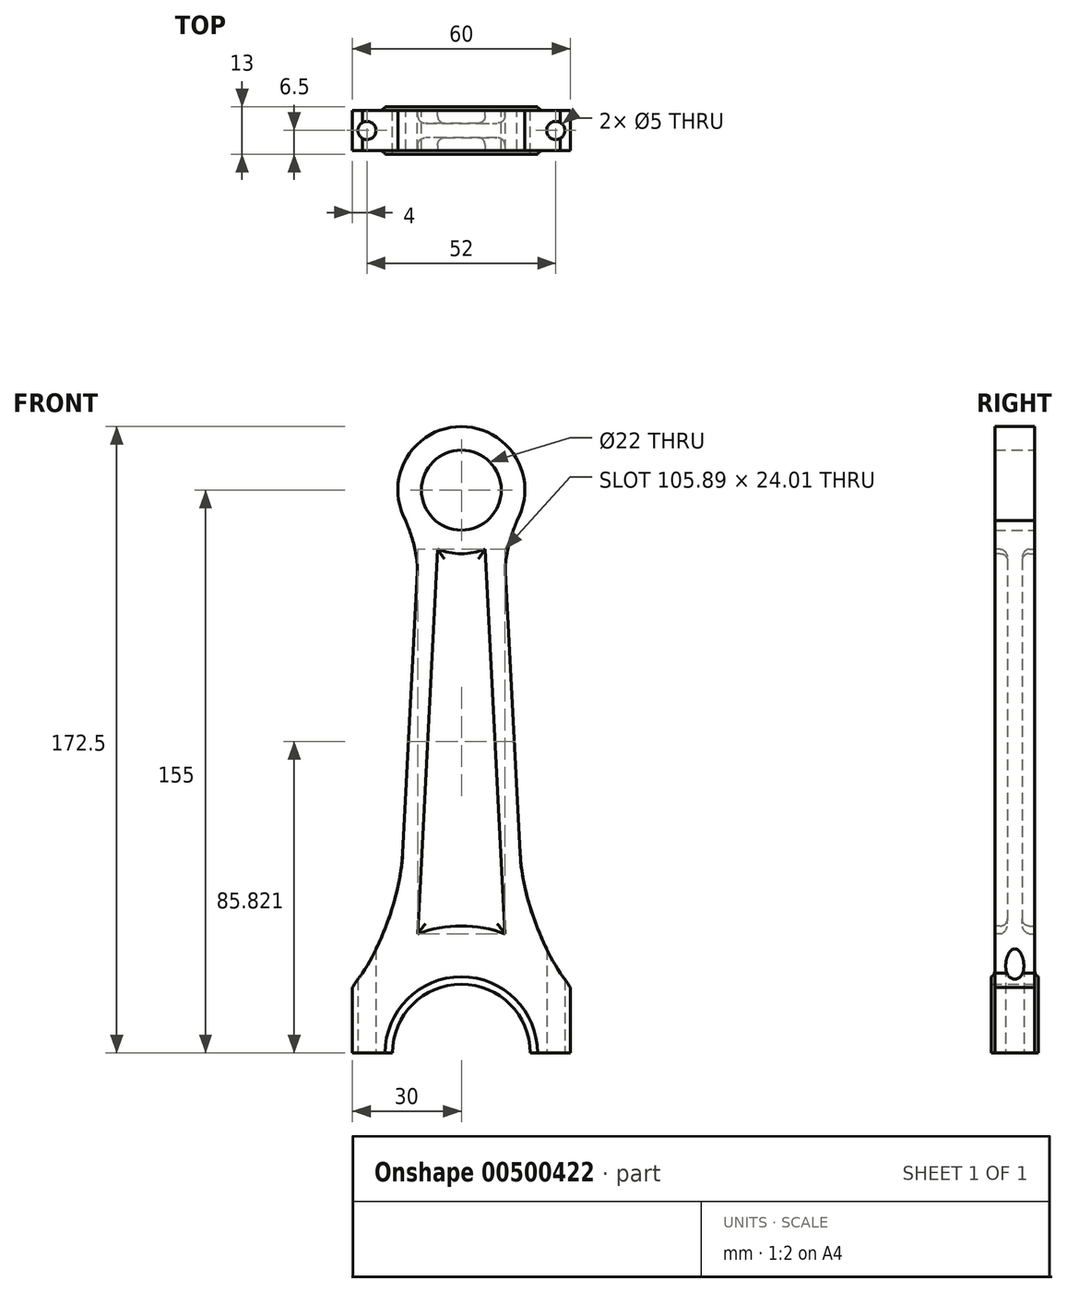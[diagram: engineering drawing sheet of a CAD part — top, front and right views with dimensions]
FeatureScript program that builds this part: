
annotation { "Feature Type Name" : "Feature", "Feature Type Description" : "" }
export const myFeature = defineFeature(function(context is Context, id is Id, definition is map)
    precondition{}
    {
        {
            var Q0;
            Q0=qCreatedBy(makeId("Front.planeOp"),FACE);
            var sketch = newSketch(context, id + "F0", { "sketchPlane" : qUnion([Q0])});
            skCircle(sketch, "E0", {"center": v(0, 121.72) * mm, "radius": 11 * mm});
            skArc(sketch, "E1", {"start": v(19, -33.28) * mm, "mid": v(0, -14.28) * mm, "end": v(-19, -33.28) * mm});
            skLineSegment(sketch, "E2", {"start": v(-11.69, 108.7) * mm, "end": v(-17.46, -2.94) * mm});
            skLineSegment(sketch, "E3", {"start": v(11.69, 108.7) * mm, "end": v(17.46, -2.94) * mm});
            skArc(sketch, "E4", {"start": v(-17.46, -2.94) * mm, "mid": v(-24.51, -8.3) * mm, "end": v(-30, -15.25) * mm});
            skArc(sketch, "E5", {"start": v(11.69, 108.7) * mm, "mid": v(0, 139.22) * mm, "end": v(-11.69, 108.7) * mm});
            skLineSegment(sketch, "E6", {"start": v(30, -15.25) * mm, "end": v(30, -33.28) * mm});
            skLineSegment(sketch, "E7", {"start": v(-30, -15.25) * mm, "end": v(-30, -33.28) * mm});
            skLineSegment(sketch, "E8", {"start": v(-30, -33.28) * mm, "end": v(-19, -33.28) * mm});
            skArc(sketch, "E9.trimOffspring", {"start": v(30, -15.25) * mm, "mid": v(24.51, -8.3) * mm, "end": v(17.46, -2.94) * mm});
            skLineSegment(sketch, "E10.trimOffspring", {"start": v(19, -33.28) * mm, "end": v(30, -33.28) * mm});
            skFitSpline(sketch, "E11", {"points": [v(-30, -15.25) * mm, v(-16.18, 21.78) * mm], "startDerivative": vector(16.46, 20.86) * mm, "endDerivative": vector(2.31, 44.73) * mm});
            skFitSpline(sketch, "E12", {"points": [v(16.18, 21.78) * mm, v(30, -15.25) * mm], "startDerivative": vector(2.31, -44.73) * mm, "endDerivative": vector(16.46, -20.86) * mm});
            skFitSpline(sketch, "E13", {"points": [v(-16.47, 115.81) * mm, v(-12.18, 99.21) * mm], "startDerivative": vector(4.45, -9.37) * mm, "endDerivative": vector(-0.98, -18.89) * mm});
            skFitSpline(sketch, "E14", {"points": [v(12.18, 99.21) * mm, v(16.47, 115.81) * mm], "startDerivative": vector(-0.98, 18.89) * mm, "endDerivative": vector(4.45, 9.37) * mm});
            skArc(sketch, "E15", {"start": v(21, -33.28) * mm, "mid": v(0, -12.28) * mm, "end": v(-21, -33.28) * mm});
            skSolve(sketch);
        }
        {
            var Q0;
            Q0 = qSketchRegion(id + "F0", true);
            extrude(context, id + "F1", {"entities" : qUnion([Q0]), "endBound" : BoundingType.SYMMETRIC, "depth" : 11 * mm});
        }
        {
            var Q0;
            Q0=makeQuery(id+"F1.opExtrude","CAP_FACE",FACE,{"disambiguationData":[OSD([sQuery(id+"F0.wireOp",EDGE,"E0"),sQuery(id+"F0.wireOp",EDGE,"E1"),sQuery(id+"F0.wireOp",EDGE,"E2"),sQuery(id+"F0.wireOp",EDGE,"E3"),sQuery(id+"F0.wireOp",EDGE,"E4"),sQuery(id+"F0.wireOp",EDGE,"E5"),sQuery(id+"F0.wireOp",EDGE,"E6"),sQuery(id+"F0.wireOp",EDGE,"E7"),sQuery(id+"F0.wireOp",EDGE,"E8"),sQuery(id+"F0.wireOp",EDGE,"E9.trimOffspring"),sQuery(id+"F0.wireOp",EDGE,"E10.trimOffspring"),sQuery(id+"F0.wireOp",EDGE,"E11"),sQuery(id+"F0.wireOp",EDGE,"E12"),sQuery(id+"F0.wireOp",EDGE,"E13"),sQuery(id+"F0.wireOp",EDGE,"E14")])],"isStart":false});
            var sketch = newSketch(context, id + "F2", { "sketchPlane" : qUnion([Q0])});
            skArc(sketch, "E16", {"start": v(-6.53, 105.48) * mm, "mid": v(0, 104.22) * mm, "end": v(6.53, 105.48) * mm});
            skArc(sketch, "E17", {"start": v(12, -0.4) * mm, "mid": v(0, 1.72) * mm, "end": v(-12, -0.4) * mm});
            skLineSegment(sketch, "E18", {"start": v(6.53, 105.48) * mm, "end": v(12, -0.4) * mm});
            skLineSegment(sketch, "E19", {"start": v(-6.53, 105.48) * mm, "end": v(-12, -0.4) * mm});
            skSolve(sketch);
        }
        {
            var Q0;
            Q0=makeQuery(id+"F2.imprint","IMPRINT",FACE,{"disambiguationData":[TD([[makeQuery(id+"F2.imprint","IMPRINT",EDGE,{"derivedFrom":sQuery(id+"F2.wireOp",EDGE,"E16")}),-1.0]])]});
            extrude(context, id + "F3", {"entities" : qUnion([Q0]), "operationType" : NewBodyOperationType.REMOVE, "oppositeDirection" : true, "depth" : 3.5 * mm});
        }
        {
            var Q0;
            Q0=makeQuery(id+"F1.opExtrude","CAP_FACE",FACE,{"disambiguationData":[OSD([sQuery(id+"F0.wireOp",EDGE,"E0"),sQuery(id+"F0.wireOp",EDGE,"E1"),sQuery(id+"F0.wireOp",EDGE,"E2"),sQuery(id+"F0.wireOp",EDGE,"E3"),sQuery(id+"F0.wireOp",EDGE,"E4"),sQuery(id+"F0.wireOp",EDGE,"E5"),sQuery(id+"F0.wireOp",EDGE,"E6"),sQuery(id+"F0.wireOp",EDGE,"E7"),sQuery(id+"F0.wireOp",EDGE,"E8"),sQuery(id+"F0.wireOp",EDGE,"E9.trimOffspring"),sQuery(id+"F0.wireOp",EDGE,"E10.trimOffspring"),sQuery(id+"F0.wireOp",EDGE,"E11"),sQuery(id+"F0.wireOp",EDGE,"E12"),sQuery(id+"F0.wireOp",EDGE,"E13"),sQuery(id+"F0.wireOp",EDGE,"E14")])],"isStart":true});
            var sketch = newSketch(context, id + "F4", { "sketchPlane" : qUnion([Q0])});
            skArc(sketch, "E20", {"start": v(-6.53, 105.48) * mm, "mid": v(0, 104.22) * mm, "end": v(6.53, 105.48) * mm});
            skArc(sketch, "E21", {"start": v(12, -0.4) * mm, "mid": v(0, 1.72) * mm, "end": v(-12, -0.4) * mm});
            skLineSegment(sketch, "E22", {"start": v(6.53, 105.48) * mm, "end": v(12, -0.4) * mm});
            skLineSegment(sketch, "E23", {"start": v(-6.53, 105.48) * mm, "end": v(-12, -0.4) * mm});
            skSolve(sketch);
        }
        {
            var Q0;
            Q0=makeQuery(id+"F4.imprint","IMPRINT",FACE,{"disambiguationData":[TD([[makeQuery(id+"F4.imprint","IMPRINT",EDGE,{"derivedFrom":sQuery(id+"F4.wireOp",EDGE,"E20")}),-1.0]])]});
            extrude(context, id + "F5", {"entities" : qUnion([Q0]), "operationType" : NewBodyOperationType.REMOVE, "oppositeDirection" : true, "depth" : 3.5 * mm});
        }
        {
            var Q0;
            Q0=makeQuery(id+"F1.opExtrude","SWEPT_FACE",FACE,{"disambiguationData":[OSD([sQuery(id+"F0.wireOp",EDGE,"E8")])]});
            var sketch = newSketch(context, id + "F6", { "sketchPlane" : qUnion([Q0])});
            skCircle(sketch, "E24", {"center": v(-26, 0) * mm, "radius": 2.5 * mm});
            skCircle(sketch, "E25", {"center": v(26, 0) * mm, "radius": 2.5 * mm});
            skSolve(sketch);
        }
        {
            var Q0;
            Q0=makeQuery(id+"F6.imprint","IMPRINT",FACE,{"disambiguationData":[TD([[makeQuery(id+"F6.imprint","IMPRINT",EDGE,{"derivedFrom":sQuery(id+"F6.wireOp",EDGE,"E24")}),1.0]])]});
            var Q1;
            Q1=makeQuery(id+"F6.imprint","IMPRINT",FACE,{"disambiguationData":[TD([[makeQuery(id+"F6.imprint","IMPRINT",EDGE,{"derivedFrom":sQuery(id+"F6.wireOp",EDGE,"E25")}),1.0]])]});
            extrude(context, id + "F7", {"entities" : qUnion([Q0, Q1]), "operationType" : NewBodyOperationType.REMOVE, "oppositeDirection" : true, "depth" : 42.16 * mm});
        }
        {
            var Q0;
            {var subQ0=sQuery(id+"F0.wireOp",EDGE,"E1");Q0=makeQuery(id+"F0.imprint","IMPRINT",FACE,{"disambiguationData":[TD([[makeQuery(id+"F0.imprint","IMPRINT",EDGE,{"derivedFrom":subQ0}),-1.0]])]});}
            extrude(context, id + "F8", {"entities" : qUnion([Q0]), "operationType" : NewBodyOperationType.ADD, "endBound" : BoundingType.SYMMETRIC, "depth" : 13 * mm});
        }
        {
            var Q0;
            Q0=makeQuery(id+"F8.boolean.opBoolean","INTERSECT",EDGE,{"derivedFrom":[makeQuery(id+"F1.opExtrude","CAP_FACE",FACE,{"disambiguationData":[OSD([sQuery(id+"F0.wireOp",EDGE,"E0"),sQuery(id+"F0.wireOp",EDGE,"E1"),sQuery(id+"F0.wireOp",EDGE,"E2"),sQuery(id+"F0.wireOp",EDGE,"E3"),sQuery(id+"F0.wireOp",EDGE,"E4"),sQuery(id+"F0.wireOp",EDGE,"E5"),sQuery(id+"F0.wireOp",EDGE,"E6"),sQuery(id+"F0.wireOp",EDGE,"E7"),sQuery(id+"F0.wireOp",EDGE,"E8"),sQuery(id+"F0.wireOp",EDGE,"E9.trimOffspring"),sQuery(id+"F0.wireOp",EDGE,"E10.trimOffspring"),sQuery(id+"F0.wireOp",EDGE,"E11"),sQuery(id+"F0.wireOp",EDGE,"E12"),sQuery(id+"F0.wireOp",EDGE,"E13"),sQuery(id+"F0.wireOp",EDGE,"E14")])],"isStart":false}),makeQuery(id+"F8.opExtrude","SWEPT_FACE",FACE,{"disambiguationData":[OSD([sQuery(id+"F0.wireOp",EDGE,"E15")])]})]});
            var Q1;
            Q1=makeQuery(id+"F8.boolean.opBoolean","INTERSECT",EDGE,{"derivedFrom":[makeQuery(id+"F1.opExtrude","CAP_FACE",FACE,{"disambiguationData":[OSD([sQuery(id+"F0.wireOp",EDGE,"E0"),sQuery(id+"F0.wireOp",EDGE,"E1"),sQuery(id+"F0.wireOp",EDGE,"E2"),sQuery(id+"F0.wireOp",EDGE,"E3"),sQuery(id+"F0.wireOp",EDGE,"E4"),sQuery(id+"F0.wireOp",EDGE,"E5"),sQuery(id+"F0.wireOp",EDGE,"E6"),sQuery(id+"F0.wireOp",EDGE,"E7"),sQuery(id+"F0.wireOp",EDGE,"E8"),sQuery(id+"F0.wireOp",EDGE,"E9.trimOffspring"),sQuery(id+"F0.wireOp",EDGE,"E10.trimOffspring"),sQuery(id+"F0.wireOp",EDGE,"E11"),sQuery(id+"F0.wireOp",EDGE,"E12"),sQuery(id+"F0.wireOp",EDGE,"E13"),sQuery(id+"F0.wireOp",EDGE,"E14")])],"isStart":true}),makeQuery(id+"F8.opExtrude","SWEPT_FACE",FACE,{"disambiguationData":[OSD([sQuery(id+"F0.wireOp",EDGE,"E15")])]})]});
            var Q2;
            Q2=makeQuery(id+"F3.boolean.opBoolean","COPY",EDGE,{"derivedFrom":makeQuery(id+"F3.opExtrude","CAP_EDGE",EDGE,{"disambiguationData":[OSD([sQuery(id+"F2.wireOp",EDGE,"E18")])],"isStart":false})});
            var Q3;
            Q3=makeQuery(id+"F3.boolean.opBoolean","COPY",EDGE,{"derivedFrom":makeQuery(id+"F3.opExtrude","CAP_EDGE",EDGE,{"disambiguationData":[OSD([sQuery(id+"F2.wireOp",EDGE,"E17")])],"isStart":false})});
            var Q4;
            Q4=makeQuery(id+"F3.boolean.opBoolean","COPY",EDGE,{"derivedFrom":makeQuery(id+"F3.opExtrude","CAP_EDGE",EDGE,{"disambiguationData":[OSD([sQuery(id+"F2.wireOp",EDGE,"E19")])],"isStart":false})});
            var Q5;
            Q5=makeQuery(id+"F3.boolean.opBoolean","COPY",EDGE,{"derivedFrom":makeQuery(id+"F3.opExtrude","CAP_EDGE",EDGE,{"disambiguationData":[OSD([sQuery(id+"F2.wireOp",EDGE,"E16")])],"isStart":false})});
            var Q6;
            Q6=makeQuery(id+"F5.boolean.opBoolean","COPY",EDGE,{"derivedFrom":makeQuery(id+"F5.opExtrude","CAP_EDGE",EDGE,{"disambiguationData":[OSD([sQuery(id+"F4.wireOp",EDGE,"E22")])],"isStart":false})});
            var Q7;
            Q7=makeQuery(id+"F5.boolean.opBoolean","COPY",EDGE,{"derivedFrom":makeQuery(id+"F5.opExtrude","CAP_EDGE",EDGE,{"disambiguationData":[OSD([sQuery(id+"F4.wireOp",EDGE,"E20")])],"isStart":false})});
            var Q8;
            Q8=makeQuery(id+"F5.boolean.opBoolean","COPY",EDGE,{"derivedFrom":makeQuery(id+"F5.opExtrude","CAP_EDGE",EDGE,{"disambiguationData":[OSD([sQuery(id+"F4.wireOp",EDGE,"E23")])],"isStart":false})});
            var Q9;
            Q9=makeQuery(id+"F5.boolean.opBoolean","COPY",EDGE,{"derivedFrom":makeQuery(id+"F5.opExtrude","CAP_EDGE",EDGE,{"disambiguationData":[OSD([sQuery(id+"F4.wireOp",EDGE,"E21")])],"isStart":false})});
            fillet(context, id + "F9", {"entities" : qUnion([Q0, Q1, Q2, Q3, Q4, Q5, Q6, Q7, Q8, Q9]), "radius" : 2 * mm, "tangentPropagation" : true, "allowEdgeOverflow" : false});
        }
    });
